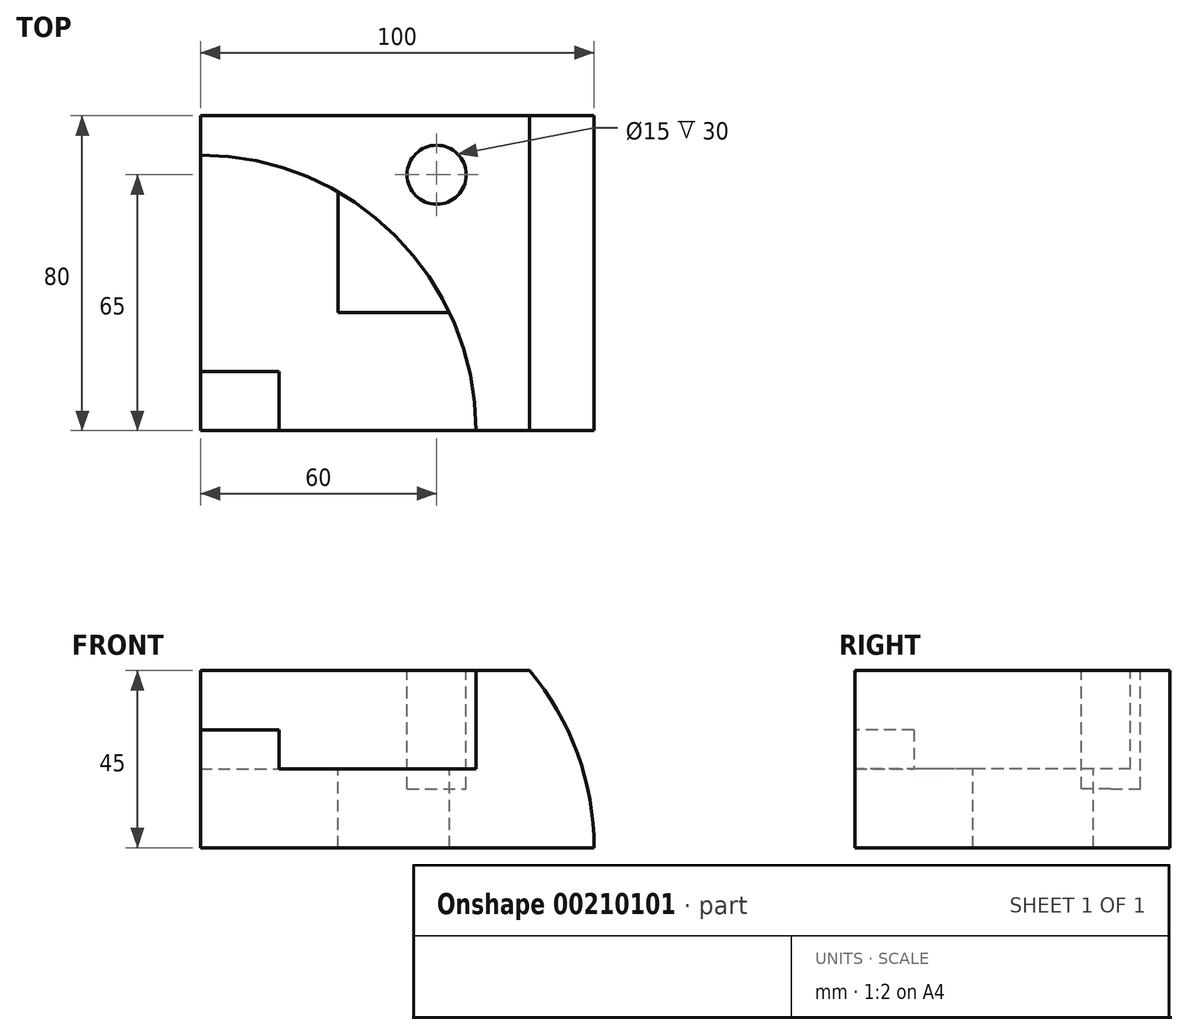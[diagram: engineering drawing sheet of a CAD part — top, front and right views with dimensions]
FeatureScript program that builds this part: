
annotation { "Feature Type Name" : "Feature", "Feature Type Description" : "" }
export const myFeature = defineFeature(function(context is Context, id is Id, definition is map)
    precondition{}
    {
        {
            var Q0;
            Q0=qCreatedBy(makeId("Front.planeOp"),FACE);
            var sketch = newSketch(context, id + "F0", { "sketchPlane" : qUnion([Q0])});
            skLineSegment(sketch, "E0", {"start": v(100, 0) * mm, "end": v(0, 0) * mm});
            skLineSegment(sketch, "E1", {"start": v(0, 0) * mm, "end": v(0, 45) * mm});
            skLineSegment(sketch, "E2", {"start": v(0, 45) * mm, "end": v(83.62, 45) * mm});
            skArc(sketch, "E3", {"start": v(100, 0) * mm, "mid": v(95.78, 23.94) * mm, "end": v(83.62, 45) * mm});
            skSolve(sketch);
        }
        {
            var Q0;
            Q0 = qSketchRegion(id + "F0", true);
            extrude(context, id + "F1", {"entities" : qUnion([Q0]), "depth" : 80 * mm});
        }
        {
            var Q0;
            Q0=makeQuery(id+"F1.opExtrude","SWEPT_FACE",FACE,{"disambiguationData":[OSD([sQuery(id+"F0.wireOp",EDGE,"E0")])]});
            cPlane(context, id + "F2", {"entities" : qUnion([Q0]), "cplaneType" : CPlaneType.OFFSET, "offset" : 20 * mm, "oppositeDirection" : true, "width" : 150 * mm, "height" : 150 * mm});
        }
        {
            var Q0;
            Q0=makeQuery(id+"F1.opExtrude","SWEPT_FACE",FACE,{"disambiguationData":[OSD([sQuery(id+"F0.wireOp",EDGE,"E2")])]});
            var sketch = newSketch(context, id + "F3", { "sketchPlane" : qUnion([Q0])});
            skCircle(sketch, "E4", {"center": v(0, -80) * mm, "radius": 70 * mm});
            skSolve(sketch);
        }
        {
            var Q0;
            Q0 = qSketchRegion(id + "F3", true);
            var Q1;
            Q1=qCreatedBy(id+"F2.planeOp",FACE);
            extrude(context, id + "F4", {"entities" : qUnion([Q0]), "operationType" : NewBodyOperationType.REMOVE, "endBound" : BoundingType.UP_TO_SURFACE, "oppositeDirection" : true, "endBoundEntityFace" : qUnion([Q1]), "depth" : 25 * mm});
        }
        {
            var Q0;
            Q0=makeQuery(id+"F4.boolean.opBoolean","COPY",FACE,{"derivedFrom":makeQuery(id+"F4.opExtrude","CAP_FACE",FACE,{"disambiguationData":[OSD([sQuery(id+"F3.wireOp",EDGE,"E4")])],"isStart":false})});
            var sketch = newSketch(context, id + "F5", { "sketchPlane" : qUnion([Q0])});
            skLineSegment(sketch, "E5.bottom", {"start": v(0, -80) * mm, "end": v(20, -80) * mm});
            skLineSegment(sketch, "E5.top", {"start": v(0, -65) * mm, "end": v(20, -65) * mm});
            skLineSegment(sketch, "E5.left", {"start": v(0, -80) * mm, "end": v(0, -65) * mm});
            skLineSegment(sketch, "E5.right", {"start": v(20, -80) * mm, "end": v(20, -65) * mm});
            skSolve(sketch);
        }
        {
            var Q0;
            Q0 = qSketchRegion(id + "F5", true);
            extrude(context, id + "F6", {"entities" : qUnion([Q0]), "operationType" : NewBodyOperationType.ADD, "depth" : 10 * mm});
        }
        {
            var Q0;
            Q0=makeQuery(id+"F4.boolean.opBoolean","COPY",FACE,{"derivedFrom":makeQuery(id+"F4.opExtrude","CAP_FACE",FACE,{"disambiguationData":[OSD([sQuery(id+"F3.wireOp",EDGE,"E4")])],"isStart":false})});
            var sketch = newSketch(context, id + "F7", { "sketchPlane" : qUnion([Q0])});
            skLineSegment(sketch, "E6", {"start": v(35, -19.38) * mm, "end": v(35, -50) * mm});
            skLineSegment(sketch, "E7", {"start": v(35, -50) * mm, "end": v(63.25, -50) * mm});
            skArc(sketch, "E8", {"start": v(63.25, -50) * mm, "mid": v(51.45, -32.54) * mm, "end": v(35, -19.38) * mm});
            skSolve(sketch);
        }
        {
            var Q0;
            Q0 = qSketchRegion(id + "F7", true);
            extrude(context, id + "F8", {"entities" : qUnion([Q0]), "operationType" : NewBodyOperationType.REMOVE, "endBound" : BoundingType.THROUGH_ALL, "oppositeDirection" : true, "depth" : 25 * mm});
        }
        {
            var Q0;
            Q0=makeQuery(id+"F1.opExtrude","SWEPT_FACE",FACE,{"disambiguationData":[OSD([sQuery(id+"F0.wireOp",EDGE,"E0")])]});
            cPlane(context, id + "F9", {"entities" : qUnion([Q0]), "cplaneType" : CPlaneType.OFFSET, "offset" : 15 * mm, "oppositeDirection" : true, "width" : 150 * mm, "height" : 150 * mm});
        }
        {
            var Q0;
            Q0=makeQuery(id+"F1.opExtrude","SWEPT_FACE",FACE,{"disambiguationData":[OSD([sQuery(id+"F0.wireOp",EDGE,"E2")])]});
            var sketch = newSketch(context, id + "F10", { "sketchPlane" : qUnion([Q0])});
            skCircle(sketch, "E9", {"center": v(60, -15) * mm, "radius": 7.5 * mm});
            skSolve(sketch);
        }
        {
            var Q0;
            Q0 = qSketchRegion(id + "F10", true);
            var Q1;
            Q1=qCreatedBy(id+"F9.planeOp",FACE);
            extrude(context, id + "F11", {"entities" : qUnion([Q0]), "operationType" : NewBodyOperationType.REMOVE, "endBound" : BoundingType.UP_TO_SURFACE, "oppositeDirection" : true, "endBoundEntityFace" : qUnion([Q1]), "depth" : 25 * mm});
        }
    });
